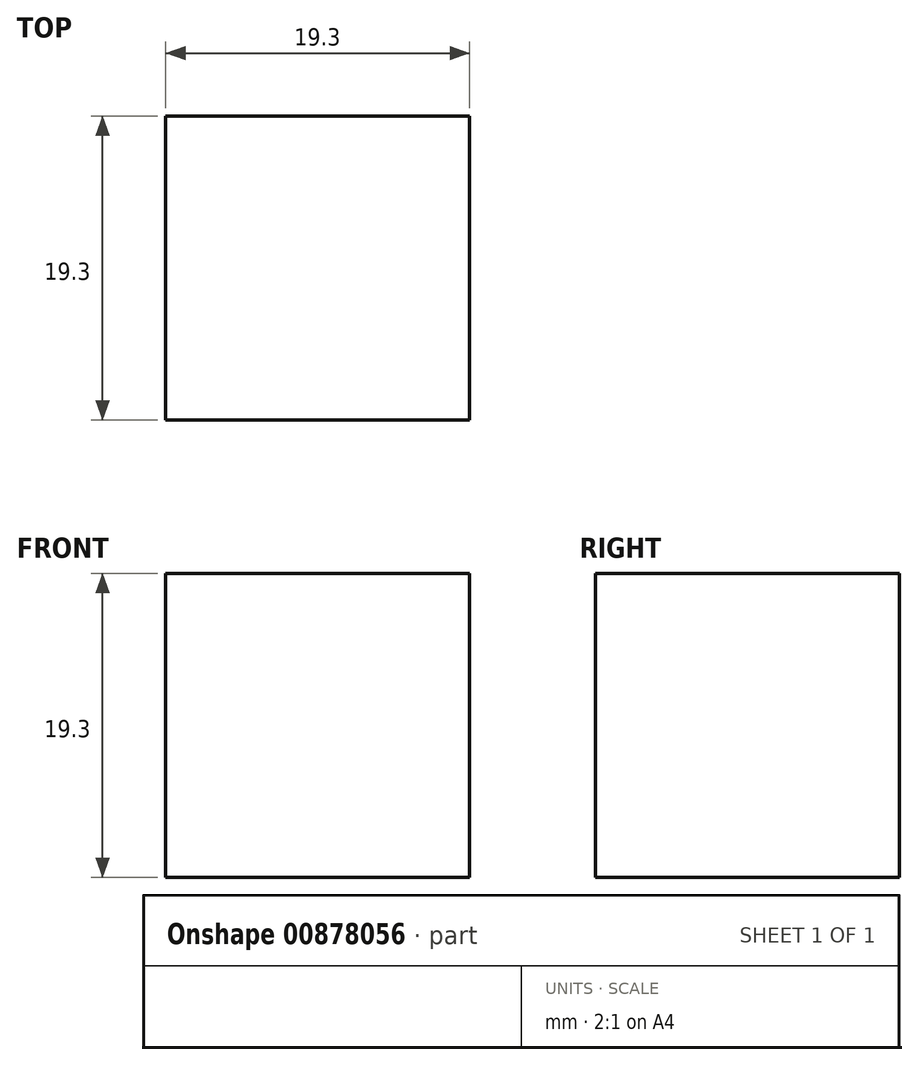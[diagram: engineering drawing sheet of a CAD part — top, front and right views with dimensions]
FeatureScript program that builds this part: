
annotation { "Feature Type Name" : "Feature", "Feature Type Description" : "" }
export const myFeature = defineFeature(function(context is Context, id is Id, definition is map)
    precondition{}
    {
        {
            var Q0;
            Q0=qCreatedBy(makeId("Front.planeOp"),FACE);
            var sketch = newSketch(context, id + "F0", { "sketchPlane" : qUnion([Q0])});
            skLineSegment(sketch, "E0.bottom", {"start": v(-9.65, 9.65) * mm, "end": v(9.65, 9.65) * mm});
            skLineSegment(sketch, "E0.top", {"start": v(-9.65, -9.65) * mm, "end": v(9.65, -9.65) * mm});
            skLineSegment(sketch, "E0.left", {"start": v(-9.65, 9.65) * mm, "end": v(-9.65, -9.65) * mm});
            skLineSegment(sketch, "E0.right", {"start": v(9.65, 9.65) * mm, "end": v(9.65, -9.65) * mm});
            skPoint(sketch, "E0.middle", {"position": v(0, 0) * mm});
            skSolve(sketch);
        }
        {
            var Q0;
            Q0 = qSketchRegion(id + "F0", true);
            extrude(context, id + "F1", {"entities" : qUnion([Q0]), "depth" : 19.3 * mm, "offsetDistance" : 25.4 * mm});
        }
    });
